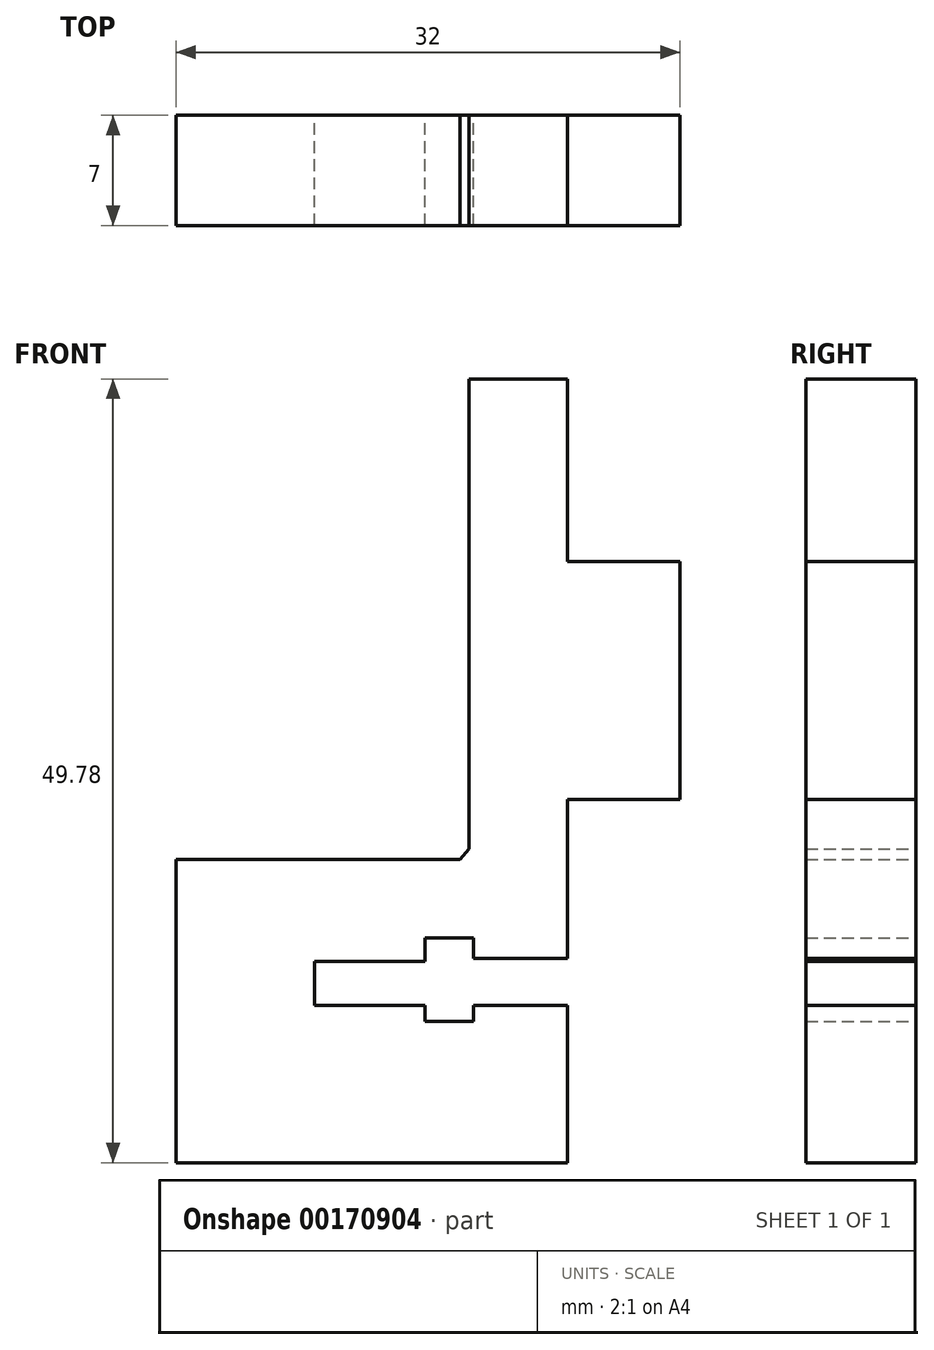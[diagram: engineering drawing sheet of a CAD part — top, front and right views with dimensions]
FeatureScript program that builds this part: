
annotation { "Feature Type Name" : "Feature", "Feature Type Description" : "" }
export const myFeature = defineFeature(function(context is Context, id is Id, definition is map)
    precondition{}
    {
        {
            var Q0;
            Q0=qCreatedBy(makeId("Front.planeOp"),FACE);
            var sketch = newSketch(context, id + "F0", { "sketchPlane" : qUnion([Q0])});
            skLineSegment(sketch, "E0", {"start": v(-14.56, 55.95) * mm, "end": v(-8.3, 55.95) * mm});
            skLineSegment(sketch, "E1", {"start": v(-8.3, 55.95) * mm, "end": v(-8.3, 44.35) * mm});
            skLineSegment(sketch, "E2", {"start": v(-8.3, 44.35) * mm, "end": v(-1.16, 44.35) * mm});
            skLineSegment(sketch, "E3", {"start": v(-1.16, 44.35) * mm, "end": v(-1.16, 29.25) * mm});
            skLineSegment(sketch, "E4", {"start": v(-1.16, 29.25) * mm, "end": v(-8.3, 29.25) * mm});
            skLineSegment(sketch, "E5", {"start": v(-8.3, 29.25) * mm, "end": v(-8.3, 19.15) * mm});
            skLineSegment(sketch, "E6", {"start": v(-8.3, 19.15) * mm, "end": v(-14.26, 19.15) * mm});
            skLineSegment(sketch, "E7", {"start": v(-14.26, 19.15) * mm, "end": v(-14.26, 20.44) * mm});
            skLineSegment(sketch, "E8", {"start": v(-14.26, 20.44) * mm, "end": v(-17.36, 20.44) * mm});
            skLineSegment(sketch, "E9", {"start": v(-17.36, 20.44) * mm, "end": v(-17.36, 18.95) * mm});
            skLineSegment(sketch, "E10", {"start": v(-17.36, 18.95) * mm, "end": v(-24.36, 18.95) * mm});
            skLineSegment(sketch, "E11", {"start": v(-24.36, 18.95) * mm, "end": v(-24.36, 16.15) * mm});
            skLineSegment(sketch, "E12", {"start": v(-24.36, 16.15) * mm, "end": v(-17.36, 16.15) * mm});
            skLineSegment(sketch, "E13", {"start": v(-17.36, 16.15) * mm, "end": v(-17.36, 15.15) * mm});
            skLineSegment(sketch, "E14", {"start": v(-17.36, 15.15) * mm, "end": v(-14.26, 15.15) * mm});
            skLineSegment(sketch, "E15", {"start": v(-14.26, 15.15) * mm, "end": v(-14.26, 16.15) * mm});
            skLineSegment(sketch, "E16", {"start": v(-14.26, 16.15) * mm, "end": v(-8.3, 16.15) * mm});
            skLineSegment(sketch, "E17", {"start": v(-8.3, 16.15) * mm, "end": v(-8.3, 6.17) * mm});
            skLineSegment(sketch, "E18", {"start": v(-8.3, 6.17) * mm, "end": v(-33.16, 6.17) * mm});
            skLineSegment(sketch, "E19", {"start": v(-33.16, 6.17) * mm, "end": v(-33.16, 25.44) * mm});
            skLineSegment(sketch, "E20", {"start": v(-33.16, 25.44) * mm, "end": v(-15.14, 25.44) * mm});
            skLineSegment(sketch, "E21", {"start": v(-14.56, 26.1) * mm, "end": v(-14.56, 55.95) * mm});
            skLineSegment(sketch, "E22", {"start": v(-15.14, 25.44) * mm, "end": v(-14.56, 26.1) * mm});
            skLineSegment(sketch, "E23", {"start": v(-25.72, 17.55) * mm, "end": v(-3.73, 17.55) * mm, "construction": true});
            skSolve(sketch);
        }
        {
            var Q0;
            Q0=makeQuery(id+"F0.imprint","IMPRINT",FACE,{"disambiguationData":[TD([[makeQuery(id+"F0.imprint","IMPRINT",EDGE,{"derivedFrom":sQuery(id+"F0.wireOp",EDGE,"E0")}),-1.0]])]});
            extrude(context, id + "F1", {"entities" : qUnion([Q0]), "depth" : 7 * mm});
        }
    });
